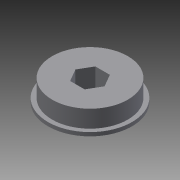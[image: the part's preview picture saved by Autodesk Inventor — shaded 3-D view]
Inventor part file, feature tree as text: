
AUTODESK INVENTOR PART (.ipt)
format: ipt  version: 2013 (Build 170138000, 138)  size: 98,816 bytes
history: native  units: in
note: dims shown in document units (in); Inventor stores cm internally (conversion verified against a paired STEP export)
features: extrude x2, sketch x2
ambient origin geometry x8: Origin, YZ Plane, XZ Plane, XY Plane, X Axis, Y Axis, Z Axis, Center Point
bodies: Solid1 (feature_tree)
feature tree (4):
  extrude  "Extrusion1"  Depth=0.055in TaperAngle=0.0deg
  extrude  "Extrusion2"  Depth=0.257in TaperAngle=0.0deg
  sketch  "Sketch1"  dims[d0=1.25in d4=0.055in d5=0.0in]
  sketch  "Sketch2"  dims[d6=1.125in d7=0.257in d8=0.0in d9=0.375in]
